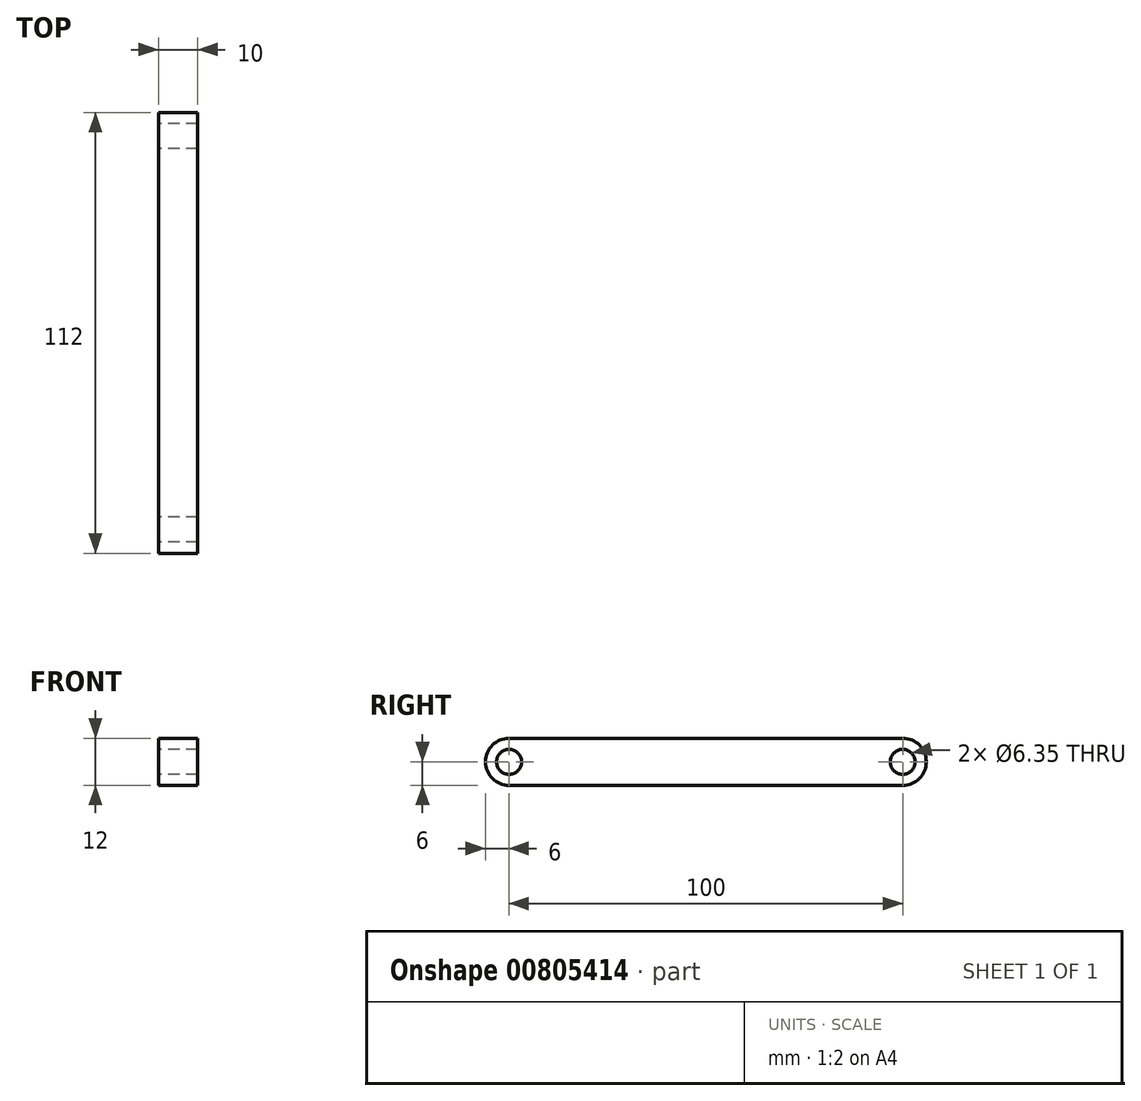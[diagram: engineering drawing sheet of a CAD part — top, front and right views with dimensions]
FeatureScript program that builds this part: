
annotation { "Feature Type Name" : "Feature", "Feature Type Description" : "" }
export const myFeature = defineFeature(function(context is Context, id is Id, definition is map)
    precondition{}
    {
        {
            var Q0;
            Q0=qCreatedBy(makeId("Right.planeOp"),FACE);
            var sketch = newSketch(context, id + "F0", { "sketchPlane" : qUnion([Q0])});
            skLineSegment(sketch, "E0.bottom", {"start": v(-50, 6) * mm, "end": v(50, 6) * mm});
            skLineSegment(sketch, "E0.top", {"start": v(-50, -6) * mm, "end": v(50, -6) * mm});
            skPoint(sketch, "E0.middle", {"position": v(0, 0) * mm});
            skPoint(sketch, "E1", {"position": v(-50, 0) * mm});
            skPoint(sketch, "E2", {"position": v(50, 0) * mm});
            skArc(sketch, "E3", {"start": v(-50, 6) * mm, "mid": v(-56, 0) * mm, "end": v(-50, -6) * mm});
            skArc(sketch, "E4", {"start": v(50, 6) * mm, "mid": v(56, 0) * mm, "end": v(50, -6) * mm});
            skCircle(sketch, "E5", {"center": v(-50, 0) * mm, "radius": 3.17 * mm});
            skCircle(sketch, "E6", {"center": v(50, 0) * mm, "radius": 3.17 * mm});
            skSolve(sketch);
        }
        {
            var Q0;
            Q0 = qSketchRegion(id + "F0", true);
            extrude(context, id + "F1", {"entities" : qUnion([Q0]), "depth" : 10 * mm, "offsetDistance" : 25 * mm});
        }
    });
